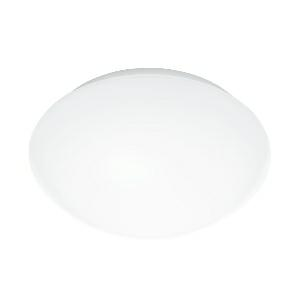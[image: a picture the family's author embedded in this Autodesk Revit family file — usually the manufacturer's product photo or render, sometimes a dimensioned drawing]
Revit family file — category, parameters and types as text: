
# Revit family: rs_pro_led_p1_sl_056056
name_source: partatom
category: Leuchten
revit_build: Autodesk Revit 2016 (Build: 20190508_0715(x64)
units: mm (PartAtom-declared; Revit-internal decimal feet)

## family parameters
Basisbauteil = Fläche
Beim Laden mit Abzugskörper schneiden = Nein
Bemaßung runder Anschluss = Durchmesser verwenden
Gemeinsam genutzt = Nein
Lichtquelle = Nein
Raumberechnungspunkt = Nein
Teiletyp = Normal

## types (1)
- RS PRO LED P1 SL (1 x , 960 lm, 3000 K)
    Beschreibung = Dimensions (Ø x H): 280 x 110 mm; Mains power supply: 220 – 240 V / 50 – 60 Hz; Output: 9 W; Luminous flux: 960 lm; Colour temperature: 3000 K; Colour variation LED: SDCM3; Colour Rendering Index CRI: 80-89; With lamp: Yes, STEINEL LED system; Lamp: LED cannot be replaced; LED life expectancy (max. °C): 50000 h; Drop in luminous flux in accordance with LM80: L80B10; Base: without; LED cooling system: Passive Thermo Control; With motion detector: No; Photo-cell controller: No; Basic light level function: No; Soft light start: Yes; Impact resistance: IK03; IP-rating: IP54; Protection class: II; Ambient temperature: 10 – 40 °C; Housing material: Plastic; Cover material: Plastic, opal; Manufacturer's Warranty: 5 years; With remote control: No; Version: warm white; PU1, EAN: 4007841056056
    CIE Flux Codes = 41 70 89 89 100
    Color Rendering = 80-89
    Color Temperature = 3000 K
    Frequency = 60 Hz, 50 Hz
    Height = 0 mm  [stored 0 ft]
    Hersteller = Steinel
    Lamp Light Flux = 960 lm
    Lamp count = 1
    Lampe = 1 x
    Length = 280 mm
    Luminous efficacy = 107 lm/W
    ModVariant = Nein
    Modell = 056056
    Mounting Type = Surface mounted
    Number of Poles = 1
    OnlyDefault = Ja
    Power Factor = 1
    Product Name = RS PRO LED P1 SL
    Product group = Sensor-switched indoor light
    ProductGroupID = 30
    Protection Class = Protection class II
    Protection Degree = IP 54
    RlxData = <blob elided: 60629 chars, md5=f34898d6>
    Scheinlast = 9 VA
    Socket = socket
    Standby Power = 0 W
    System Light Flux = 960 lm
    System Power = 9 W
    Typenbild = produkt1_056056.jpg
    Typenkommentare = Product without accessories
    URL = http://relux.com
    VarID = ---
    Voltage = 0 V
    Vorgabe-Ansicht = 1800 mm
    Weight = 0.00 kg
    Width = 0 mm  [stored 0 ft]

note: [stored X ft] marks values corroborated as IEEE doubles in the binary element streams (Revit-internal decimal feet)

## geometry (parser evidence)
native form markers: Blend x4, Sweep x17
no freeform markers — native parametric forms only
